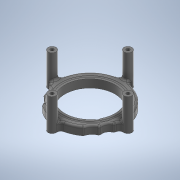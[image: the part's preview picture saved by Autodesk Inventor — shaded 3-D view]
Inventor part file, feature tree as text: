
AUTODESK INVENTOR PART (.ipt)
format: ipt  version: 2020 (Build 240168000, 168)  size: 418,304 bytes
history: native  units: in
note: dims shown in document units (in); Inventor stores cm internally (conversion verified against a paired STEP export)
features: sketch x4, extrude x3, revolve x1, fillet x1
ambient origin geometry x8: Origin, YZ Plane, XZ Plane, XY Plane, X Axis, Y Axis, Z Axis, Center Point
bodies: Solid1 (feature_tree)
feature tree (9):
  extrude  "Extrusion1"  Depth=0.505in TaperAngle=0.0deg
  revolve  "Revolution1"  [1 undecoded]
  extrude  "Extrusion2"  TaperAngle=90.0deg  [1 undecoded]
  extrude  "Extrusion7"  Depth=0.5in
  fillet  "Fillet6"  Radius=0.2031in
  sketch  "Sketch1"  dims[d0=4.25in d1=0.505in d2=0.0in]
  sketch  "Sketch2"  dims[d3=0.125in d4=1.75in]
  sketch  "Sketch3"  dims[d5=0.02in d6=90.0deg]
  sketch  "Sketch6"  dims[d7=3.125in d8=0.5in d9=0.2031in d10=1.5748in d12=360.0deg d14=2.0in d15=0.0in d50=1.8in d51=2.727in d52=2.0in d53=0.0in d54=0.0in d56=0.375in d57=0.125in d59=0.7in d60=1.3in d45=0.5in d46=0.0344in d47=0.5in d48=0.0344in]
note: 2 required parameter values undecoded (feature->parameter linkage not recoverable at this tier; creation-order binding heuristic only, values carry confidence <= 0.55)